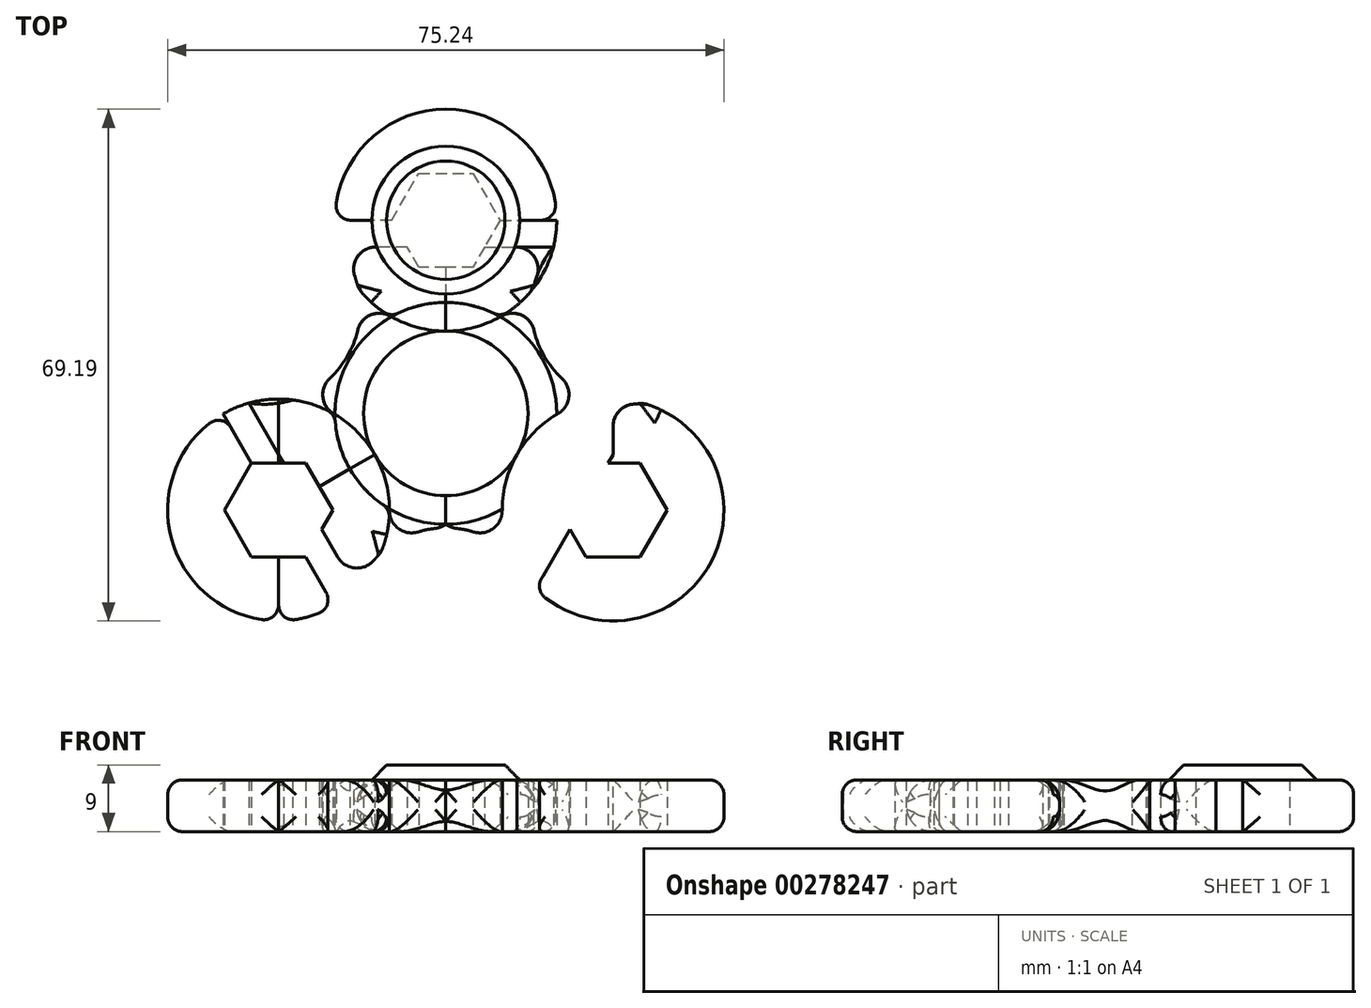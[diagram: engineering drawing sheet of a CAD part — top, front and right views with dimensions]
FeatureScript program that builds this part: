
annotation { "Feature Type Name" : "Feature", "Feature Type Description" : "" }
export const myFeature = defineFeature(function(context is Context, id is Id, definition is map)
    precondition{}
    {
        {
            var Q0;
            Q0=qCreatedBy(makeId("Top.planeOp"),FACE);
            var sketch = newSketch(context, id + "F0", { "sketchPlane" : qUnion([Q0])});
            skCircle(sketch, "E0", {"center": v(0, 26.12) * mm, "radius": 15 * mm});
            skLineSegment(sketch, "E1", {"start": v(0, 26.12) * mm, "end": v(0, -26.13) * mm});
            skLineSegment(sketch, "E2", {"start": v(0, 11.12) * mm, "end": v(0, 0) * mm});
            skCircle(sketch, "E3", {"center": v(0, 0) * mm, "radius": 15 * mm});
            skCircle(sketch, "E4", {"center": v(0, 0) * mm, "radius": 11.12 * mm});
            skCircle(sketch, "E5.1.1", {"center": v(-22.62, -13.06) * mm, "radius": 15 * mm});
            skCircle(sketch, "E5.2.1", {"center": v(22.62, -13.06) * mm, "radius": 15 * mm});
            skLineSegment(sketch, "E6", {"start": v(-22.62, -13.06) * mm, "end": v(-22.62, 15.78) * mm});
            skLineSegment(sketch, "E7", {"start": v(0, 26.12) * mm, "end": v(-15, 26.12) * mm});
            skLineSegment(sketch, "E8", {"start": v(-15, 26.12) * mm, "end": v(0, 26.12) * mm});
            skLineSegment(sketch, "E9", {"start": v(0, 26.12) * mm, "end": v(15, 26.12) * mm});
            skLineSegment(sketch, "E10", {"start": v(-22.62, -13.06) * mm, "end": v(-22.62, -28.06) * mm});
            skLineSegment(sketch, "E11", {"start": v(22.62, -13.06) * mm, "end": v(22.62, -28.06) * mm});
            skLineSegment(sketch, "E12", {"start": v(22.62, -28.06) * mm, "end": v(22.62, -13.06) * mm});
            skLineSegment(sketch, "E13", {"start": v(22.62, 1.94) * mm, "end": v(22.62, -13.06) * mm});
            skLineSegment(sketch, "E14", {"start": v(-22.62, -13.06) * mm, "end": v(-9.63, -5.56) * mm});
            skLineSegment(sketch, "E15", {"start": v(22.62, -13.06) * mm, "end": v(9.63, -5.56) * mm});
            skLineSegment(sketch, "E16", {"start": v(9.63, -5.56) * mm, "end": v(22.62, -13.06) * mm});
            skLineSegment(sketch, "E17", {"start": v(22.62, -13.06) * mm, "end": v(15.12, -26.05) * mm});
            skLineSegment(sketch, "E18", {"start": v(-22.62, -13.06) * mm, "end": v(-15.12, -26.05) * mm});
            skLineSegment(sketch, "E19", {"start": v(-15.12, -26.05) * mm, "end": v(-22.62, -13.06) * mm});
            skLineSegment(sketch, "E20", {"start": v(-22.62, -13.06) * mm, "end": v(-30.12, -0.07) * mm});
            skLineSegment(sketch, "E21", {"start": v(22.62, -13.06) * mm, "end": v(30.12, -0.07) * mm});
            skLineSegment(sketch, "E22", {"start": v(0, 26.12) * mm, "end": v(-11.55, 16.56) * mm, "construction": true});
            skLineSegment(sketch, "E23", {"start": v(-11.55, 16.56) * mm, "end": v(-5.78, 21.34) * mm, "construction": true});
            skLineSegment(sketch, "E24", {"start": v(22.62, -28.06) * mm, "end": v(15.12, -26.05) * mm});
            skLineSegment(sketch, "E25", {"start": v(22.62, -13.06) * mm, "end": v(16.13, -9.31) * mm});
            skLineSegment(sketch, "E26", {"start": v(13, -7.5) * mm, "end": v(19.38, -11.19) * mm});
            skLineSegment(sketch, "E27", {"start": v(19.38, -11.19) * mm, "end": v(12.12, -23.77) * mm});
            skLineSegment(sketch, "E28", {"start": v(-13, -7.5) * mm, "end": v(-19.38, -11.19) * mm});
            skLineSegment(sketch, "E29", {"start": v(-19.38, -11.19) * mm, "end": v(-12.12, -23.77) * mm});
            skLineSegment(sketch, "E30", {"start": v(-19.38, -11.19) * mm, "end": v(-26.64, 1.4) * mm});
            skLineSegment(sketch, "E31", {"start": v(19.38, -11.19) * mm, "end": v(26.64, 1.4) * mm});
            skLineSegment(sketch, "E32", {"start": v(0, 15) * mm, "end": v(0, 22.5) * mm});
            skLineSegment(sketch, "E33", {"start": v(0, 22.5) * mm, "end": v(-14.56, 22.5) * mm});
            skLineSegment(sketch, "E34", {"start": v(0, 22.5) * mm, "end": v(14.56, 22.5) * mm});
            skArc(sketch, "E35", {"start": v(12.12, -23.77) * mm, "mid": v(0, -15.48) * mm, "end": v(-12.12, -23.77) * mm});
            skArc(sketch, "E36", {"start": v(-26.64, 1.4) * mm, "mid": v(-13.3, 7.77) * mm, "end": v(-14.56, 22.5) * mm});
            skArc(sketch, "E37", {"start": v(14.56, 22.5) * mm, "mid": v(13.3, 7.77) * mm, "end": v(26.64, 1.4) * mm});
            skCircle(sketch, "E38.cCircle", {"center": v(-22.62, -13.06) * mm, "radius": 6.35 * mm, "construction": true});
            skLineSegment(sketch, "E38.0", {"start": v(-18.96, -6.71) * mm, "end": v(-15.3, -13.06) * mm});
            skLineSegment(sketch, "E38.1", {"start": v(-15.3, -13.06) * mm, "end": v(-18.96, -19.41) * mm});
            skLineSegment(sketch, "E38.2", {"start": v(-18.96, -19.41) * mm, "end": v(-26.3, -19.41) * mm});
            skLineSegment(sketch, "E38.3", {"start": v(-26.3, -19.41) * mm, "end": v(-29.96, -13.06) * mm});
            skLineSegment(sketch, "E38.4", {"start": v(-29.96, -13.06) * mm, "end": v(-26.3, -6.71) * mm});
            skLineSegment(sketch, "E38.5", {"start": v(-26.3, -6.71) * mm, "end": v(-18.96, -6.71) * mm});
            skPoint(sketch, "E38.0.midPoint", {"position": v(-17.13, -9.89) * mm});
            skCircle(sketch, "E39.cCircle", {"center": v(22.62, -13.06) * mm, "radius": 6.35 * mm, "construction": true});
            skLineSegment(sketch, "E39.0", {"start": v(15.3, -13.06) * mm, "end": v(18.96, -6.71) * mm});
            skLineSegment(sketch, "E39.1", {"start": v(18.96, -6.71) * mm, "end": v(26.3, -6.71) * mm});
            skLineSegment(sketch, "E39.2", {"start": v(26.3, -6.71) * mm, "end": v(29.96, -13.06) * mm});
            skLineSegment(sketch, "E39.3", {"start": v(29.96, -13.06) * mm, "end": v(26.3, -19.41) * mm});
            skLineSegment(sketch, "E39.4", {"start": v(26.3, -19.41) * mm, "end": v(18.96, -19.41) * mm});
            skLineSegment(sketch, "E39.5", {"start": v(18.96, -19.41) * mm, "end": v(15.3, -13.06) * mm});
            skPoint(sketch, "E39.0.midPoint", {"position": v(17.13, -9.89) * mm});
            skCircle(sketch, "E40.cCircle", {"center": v(0, 26.12) * mm, "radius": 6.35 * mm, "construction": true});
            skLineSegment(sketch, "E40.0", {"start": v(3.67, 19.77) * mm, "end": v(-3.67, 19.77) * mm});
            skLineSegment(sketch, "E40.1", {"start": v(-3.67, 19.77) * mm, "end": v(-7.33, 26.12) * mm});
            skLineSegment(sketch, "E40.2", {"start": v(-7.33, 26.12) * mm, "end": v(-3.67, 32.47) * mm});
            skLineSegment(sketch, "E40.3", {"start": v(-3.67, 32.48) * mm, "end": v(3.67, 32.48) * mm});
            skLineSegment(sketch, "E40.4", {"start": v(3.67, 32.47) * mm, "end": v(7.33, 26.12) * mm});
            skLineSegment(sketch, "E40.5", {"start": v(7.33, 26.12) * mm, "end": v(3.67, 19.77) * mm});
            skPoint(sketch, "E40.0.midPoint", {"position": v(0, 19.77) * mm});
            skSolve(sketch);
        }
        {
            var Q0;
            {var subQ0=sQuery(id+"F0.wireOp",EDGE,"E38.5");var subQ1=sQuery(id+"F0.wireOp",EDGE,"E6");var subQ2=makeQuery(id+"F0.imprint","INTERSECT",VERTEX,{"derivedFrom":[subQ1,subQ0]});Q0=makeQuery(id+"F0.imprint","IMPRINT",FACE,{"disambiguationData":[TD([[makeQuery(id+"F0.imprint","IMPRINT",EDGE,{"disambiguationData":[TD([[subQ2,-1.0]])],"derivedFrom":subQ1}),-1.0]])]});}
            var Q1;
            {var subQ0=sQuery(id+"F0.wireOp",EDGE,"E38.3");Q1=makeQuery(id+"F0.imprint","IMPRINT",FACE,{"disambiguationData":[TD([[makeQuery(id+"F0.imprint","IMPRINT",EDGE,{"derivedFrom":subQ0}),1.0]])]});}
            var Q2;
            {var subQ5=sQuery(id+"F0.wireOp",EDGE,"E36");var subQ6=sQuery(id+"F0.wireOp",EDGE,"E5.1.1");var subQ7=makeQuery(id+"F0.imprint","INTERSECT",VERTEX,{"derivedFrom":[subQ6,subQ5]});Q2=makeQuery(id+"F0.imprint","IMPRINT",FACE,{"disambiguationData":[TD([[makeQuery(id+"F0.imprint","IMPRINT",EDGE,{"disambiguationData":[TD([[subQ7,1.0]])],"derivedFrom":subQ6}),1.0]])]});}
            var Q3;
            {var subQ5=sQuery(id+"F0.wireOp",EDGE,"E5.1.1");var subQ7=sQuery(id+"F0.wireOp",EDGE,"E35");var subQ12=makeQuery(id+"F0.imprint","INTERSECT",VERTEX,{"derivedFrom":[subQ5,subQ7]});Q3=makeQuery(id+"F0.imprint","IMPRINT",FACE,{"disambiguationData":[TD([[makeQuery(id+"F0.imprint","IMPRINT",EDGE,{"disambiguationData":[TD([[subQ12,-1.0]])],"derivedFrom":subQ5}),1.0]])]});}
            var Q4;
            {var subQ1=sQuery(id+"F0.wireOp",EDGE,"E3");var subQ3=sQuery(id+"F0.wireOp",EDGE,"E5.1.1");var subQ4=makeQuery(id+"F0.imprint","INTERSECT",VERTEX,{"disambiguationData":[OD(1.0)],"derivedFrom":[subQ1,subQ3]});Q4=makeQuery(id+"F0.imprint","IMPRINT",FACE,{"disambiguationData":[TD([[makeQuery(id+"F0.imprint","IMPRINT",EDGE,{"disambiguationData":[TD([[subQ4,1.0]])],"derivedFrom":subQ1}),1.0]])]});}
            var Q5;
            {var subQ1=sQuery(id+"F0.wireOp",EDGE,"E3");var subQ3=sQuery(id+"F0.wireOp",EDGE,"E5.1.1");var subQ4=makeQuery(id+"F0.imprint","INTERSECT",VERTEX,{"disambiguationData":[OD(0.0)],"derivedFrom":[subQ1,subQ3]});Q5=makeQuery(id+"F0.imprint","IMPRINT",FACE,{"disambiguationData":[TD([[makeQuery(id+"F0.imprint","IMPRINT",EDGE,{"disambiguationData":[TD([[subQ4,-1.0]])],"derivedFrom":subQ1}),1.0]])]});}
            var Q6;
            {var subQ1=sQuery(id+"F0.wireOp",EDGE,"E0");var subQ3=sQuery(id+"F0.wireOp",EDGE,"E3");var subQ4=makeQuery(id+"F0.imprint","INTERSECT",VERTEX,{"disambiguationData":[OD(0.0)],"derivedFrom":[subQ1,subQ3]});Q6=makeQuery(id+"F0.imprint","IMPRINT",FACE,{"disambiguationData":[TD([[makeQuery(id+"F0.imprint","IMPRINT",EDGE,{"disambiguationData":[TD([[subQ4,-1.0]])],"derivedFrom":subQ3}),1.0]])]});}
            var Q7;
            {var subQ0=sQuery(id+"F0.wireOp",EDGE,"E36");var subQ1=sQuery(id+"F0.wireOp",EDGE,"E0");var subQ2=makeQuery(id+"F0.imprint","INTERSECT",VERTEX,{"derivedFrom":[subQ1,subQ0]});Q7=makeQuery(id+"F0.imprint","IMPRINT",FACE,{"disambiguationData":[TD([[makeQuery(id+"F0.imprint","IMPRINT",EDGE,{"disambiguationData":[TD([[subQ2,-1.0]])],"derivedFrom":subQ1}),-1.0]])]});}
            var Q8;
            {var subQ5=sQuery(id+"F0.wireOp",EDGE,"E0");var subQ11=sQuery(id+"F0.wireOp",EDGE,"E36");var subQ13=makeQuery(id+"F0.imprint","INTERSECT",VERTEX,{"derivedFrom":[subQ5,subQ11]});Q8=makeQuery(id+"F0.imprint","IMPRINT",FACE,{"disambiguationData":[TD([[makeQuery(id+"F0.imprint","IMPRINT",EDGE,{"disambiguationData":[TD([[subQ13,-1.0]])],"derivedFrom":subQ5}),1.0]])]});}
            var Q9;
            {var subQ0=sQuery(id+"F0.wireOp",EDGE,"E40.2");Q9=makeQuery(id+"F0.imprint","IMPRINT",FACE,{"disambiguationData":[TD([[makeQuery(id+"F0.imprint","IMPRINT",EDGE,{"derivedFrom":subQ0}),1.0]])]});}
            var Q10;
            {var subQ1=sQuery(id+"F0.wireOp",EDGE,"E0");var subQ3=sQuery(id+"F0.wireOp",EDGE,"E3");var subQ4=makeQuery(id+"F0.imprint","INTERSECT",VERTEX,{"disambiguationData":[OD(1.0)],"derivedFrom":[subQ1,subQ3]});Q10=makeQuery(id+"F0.imprint","IMPRINT",FACE,{"disambiguationData":[TD([[makeQuery(id+"F0.imprint","IMPRINT",EDGE,{"disambiguationData":[TD([[subQ4,-1.0]])],"derivedFrom":subQ3}),1.0]])]});}
            var Q11;
            {var subQ0=sQuery(id+"F0.wireOp",EDGE,"E37");var subQ2=sQuery(id+"F0.wireOp",EDGE,"E0");var subQ12=makeQuery(id+"F0.imprint","INTERSECT",VERTEX,{"derivedFrom":[subQ2,subQ0]});Q11=makeQuery(id+"F0.imprint","IMPRINT",FACE,{"disambiguationData":[TD([[makeQuery(id+"F0.imprint","IMPRINT",EDGE,{"disambiguationData":[TD([[subQ12,1.0]])],"derivedFrom":subQ2}),1.0]])]});}
            var Q12;
            {var subQ0=sQuery(id+"F0.wireOp",EDGE,"E37");var subQ1=sQuery(id+"F0.wireOp",EDGE,"E0");var subQ2=makeQuery(id+"F0.imprint","INTERSECT",VERTEX,{"derivedFrom":[subQ1,subQ0]});Q12=makeQuery(id+"F0.imprint","IMPRINT",FACE,{"disambiguationData":[TD([[makeQuery(id+"F0.imprint","IMPRINT",EDGE,{"disambiguationData":[TD([[subQ2,1.0]])],"derivedFrom":subQ1}),-1.0]])]});}
            var Q13;
            {var subQ1=sQuery(id+"F0.wireOp",EDGE,"E0");var subQ3=sQuery(id+"F0.wireOp",EDGE,"E3");var subQ4=makeQuery(id+"F0.imprint","INTERSECT",VERTEX,{"disambiguationData":[OD(1.0)],"derivedFrom":[subQ1,subQ3]});Q13=makeQuery(id+"F0.imprint","IMPRINT",FACE,{"disambiguationData":[TD([[makeQuery(id+"F0.imprint","IMPRINT",EDGE,{"disambiguationData":[TD([[subQ4,1.0]])],"derivedFrom":subQ3}),1.0]])]});}
            var Q14;
            {var subQ0=sQuery(id+"F0.wireOp",EDGE,"E4");var subQ1=sQuery(id+"F0.wireOp",EDGE,"E1");var subQ2=makeQuery(id+"F0.imprint","INTERSECT",VERTEX,{"derivedFrom":[subQ1,subQ0]});Q14=makeQuery(id+"F0.imprint","IMPRINT",FACE,{"disambiguationData":[TD([[makeQuery(id+"F0.imprint","IMPRINT",EDGE,{"disambiguationData":[TD([[subQ2,-1.0]])],"derivedFrom":subQ1}),1.0]])]});}
            var Q15;
            {var subQ0=sQuery(id+"F0.wireOp",EDGE,"E35");var subQ1=sQuery(id+"F0.wireOp",EDGE,"E1");var subQ2=makeQuery(id+"F0.imprint","INTERSECT",VERTEX,{"derivedFrom":[subQ1,subQ0]});Q15=makeQuery(id+"F0.imprint","IMPRINT",FACE,{"disambiguationData":[TD([[makeQuery(id+"F0.imprint","IMPRINT",EDGE,{"disambiguationData":[TD([[subQ2,1.0]])],"derivedFrom":subQ1}),1.0]])]});}
            var Q16;
            {var subQ0=sQuery(id+"F0.wireOp",EDGE,"E4");var subQ1=sQuery(id+"F0.wireOp",EDGE,"E1");var subQ2=makeQuery(id+"F0.imprint","INTERSECT",VERTEX,{"derivedFrom":[subQ1,subQ0]});Q16=makeQuery(id+"F0.imprint","IMPRINT",FACE,{"disambiguationData":[TD([[makeQuery(id+"F0.imprint","IMPRINT",EDGE,{"disambiguationData":[TD([[subQ2,-1.0]])],"derivedFrom":subQ1}),-1.0]])]});}
            var Q17;
            {var subQ0=sQuery(id+"F0.wireOp",EDGE,"E35");var subQ1=sQuery(id+"F0.wireOp",EDGE,"E1");var subQ2=makeQuery(id+"F0.imprint","INTERSECT",VERTEX,{"derivedFrom":[subQ1,subQ0]});Q17=makeQuery(id+"F0.imprint","IMPRINT",FACE,{"disambiguationData":[TD([[makeQuery(id+"F0.imprint","IMPRINT",EDGE,{"disambiguationData":[TD([[subQ2,1.0]])],"derivedFrom":subQ1}),-1.0]])]});}
            var Q18;
            {var subQ0=sQuery(id+"F0.wireOp",EDGE,"E24");Q18=makeQuery(id+"F0.imprint","IMPRINT",FACE,{"disambiguationData":[TD([[makeQuery(id+"F0.imprint","IMPRINT",EDGE,{"derivedFrom":subQ0}),-1.0]])]});}
            var Q19;
            {var subQ0=sQuery(id+"F0.wireOp",EDGE,"E24");Q19=makeQuery(id+"F0.imprint","IMPRINT",FACE,{"disambiguationData":[TD([[makeQuery(id+"F0.imprint","IMPRINT",EDGE,{"derivedFrom":subQ0}),1.0]])]});}
            var Q20;
            {var subQ0=sQuery(id+"F0.wireOp",EDGE,"E16");Q20=makeQuery(id+"F0.imprint","IMPRINT",FACE,{"disambiguationData":[TD([[makeQuery(id+"F0.imprint","IMPRINT",EDGE,{"derivedFrom":subQ0}),1.0]])]});}
            var Q21;
            {var subQ0=sQuery(id+"F0.wireOp",EDGE,"E39.2");Q21=makeQuery(id+"F0.imprint","IMPRINT",FACE,{"disambiguationData":[TD([[makeQuery(id+"F0.imprint","IMPRINT",EDGE,{"derivedFrom":subQ0}),1.0]])]});}
            var Q22;
            {var subQ0=sQuery(id+"F0.wireOp",EDGE,"E26");var subQ1=makeQuery(id+"F0.imprint","IMPRINT",VERTEX,{"derivedFrom":subQ0});Q22=makeQuery(id+"F0.imprint","IMPRINT",FACE,{"disambiguationData":[TD([[makeQuery(id+"F0.imprint","IMPRINT",EDGE,{"disambiguationData":[TD([[subQ1,-1.0]])],"derivedFrom":subQ0}),-1.0]])]});}
            var Q23;
            {var subQ5=sQuery(id+"F0.wireOp",EDGE,"E26");var subQ8=makeQuery(id+"F0.imprint","IMPRINT",VERTEX,{"derivedFrom":subQ5});Q23=makeQuery(id+"F0.imprint","IMPRINT",FACE,{"disambiguationData":[TD([[makeQuery(id+"F0.imprint","IMPRINT",EDGE,{"disambiguationData":[TD([[subQ8,-1.0]])],"derivedFrom":subQ5}),1.0]])]});}
            var Q24;
            {var subQ0=sQuery(id+"F0.wireOp",EDGE,"E16");Q24=makeQuery(id+"F0.imprint","IMPRINT",FACE,{"disambiguationData":[TD([[makeQuery(id+"F0.imprint","IMPRINT",EDGE,{"derivedFrom":subQ0}),-1.0]])]});}
            var Q25;
            {var subQ0=sQuery(id+"F0.wireOp",EDGE,"E31");var subQ1=sQuery(id+"F0.wireOp",EDGE,"E13");var subQ2=makeQuery(id+"F0.imprint","INTERSECT",VERTEX,{"derivedFrom":[subQ1,subQ0]});Q25=makeQuery(id+"F0.imprint","IMPRINT",FACE,{"disambiguationData":[TD([[makeQuery(id+"F0.imprint","IMPRINT",EDGE,{"disambiguationData":[TD([[subQ2,-1.0]])],"derivedFrom":subQ1}),-1.0]])]});}
            var Q26;
            {var subQ1=sQuery(id+"F0.wireOp",EDGE,"E0");var subQ3=sQuery(id+"F0.wireOp",EDGE,"E3");var subQ4=makeQuery(id+"F0.imprint","INTERSECT",VERTEX,{"disambiguationData":[OD(0.0)],"derivedFrom":[subQ1,subQ3]});Q26=makeQuery(id+"F0.imprint","IMPRINT",FACE,{"disambiguationData":[TD([[makeQuery(id+"F0.imprint","IMPRINT",EDGE,{"disambiguationData":[TD([[subQ4,1.0]])],"derivedFrom":subQ3}),1.0]])]});}
            var Q27;
            {var subQ0=sQuery(id+"F0.wireOp",EDGE,"E19");var subQ1=sQuery(id+"F0.wireOp",EDGE,"E5.1.1");var subQ2=makeQuery(id+"F0.imprint","INTERSECT",VERTEX,{"derivedFrom":[subQ1,subQ0]});Q27=makeQuery(id+"F0.imprint","IMPRINT",FACE,{"disambiguationData":[TD([[makeQuery(id+"F0.imprint","IMPRINT",EDGE,{"disambiguationData":[TD([[subQ2,-1.0]])],"derivedFrom":subQ1}),1.0]])]});}
            var Q28;
            {var subQ0=sQuery(id+"F0.wireOp",EDGE,"E10");var subQ1=sQuery(id+"F0.wireOp",EDGE,"E5.1.1");var subQ2=makeQuery(id+"F0.imprint","INTERSECT",VERTEX,{"derivedFrom":[subQ1,subQ0]});Q28=makeQuery(id+"F0.imprint","IMPRINT",FACE,{"disambiguationData":[TD([[makeQuery(id+"F0.imprint","IMPRINT",EDGE,{"disambiguationData":[TD([[subQ2,-1.0]])],"derivedFrom":subQ1}),1.0]])]});}
            var Q29;
            {var subQ3=sQuery(id+"F0.wireOp",EDGE,"E27");var subQ5=sQuery(id+"F0.wireOp",EDGE,"E39.5");var subQ7=makeQuery(id+"F0.imprint","INTERSECT",VERTEX,{"derivedFrom":[subQ3,subQ5]});Q29=makeQuery(id+"F0.imprint","IMPRINT",FACE,{"disambiguationData":[TD([[makeQuery(id+"F0.imprint","IMPRINT",EDGE,{"disambiguationData":[TD([[subQ7,-1.0]])],"derivedFrom":subQ3}),1.0]])]});}
            var Q30;
            {var subQ0=sQuery(id+"F0.wireOp",EDGE,"E9");var subQ1=sQuery(id+"F0.wireOp",EDGE,"E0");var subQ2=makeQuery(id+"F0.imprint","INTERSECT",VERTEX,{"derivedFrom":[subQ1,subQ0]});Q30=makeQuery(id+"F0.imprint","IMPRINT",FACE,{"disambiguationData":[TD([[makeQuery(id+"F0.imprint","IMPRINT",EDGE,{"disambiguationData":[TD([[subQ2,1.0]])],"derivedFrom":subQ1}),1.0]])]});}
            var Q31;
            {var subQ0=sQuery(id+"F0.wireOp",EDGE,"E31");var subQ3=sQuery(id+"F0.wireOp",EDGE,"E13");var subQ4=makeQuery(id+"F0.imprint","INTERSECT",VERTEX,{"derivedFrom":[subQ3,subQ0]});Q31=makeQuery(id+"F0.imprint","IMPRINT",FACE,{"disambiguationData":[TD([[makeQuery(id+"F0.imprint","IMPRINT",EDGE,{"disambiguationData":[TD([[subQ4,-1.0]])],"derivedFrom":subQ3}),1.0]])]});}
            var Q32;
            {var subQ0=sQuery(id+"F0.wireOp",EDGE,"E37");var subQ1=sQuery(id+"F0.wireOp",EDGE,"E13");var subQ2=makeQuery(id+"F0.imprint","INTERSECT",VERTEX,{"derivedFrom":[subQ1,subQ0]});Q32=makeQuery(id+"F0.imprint","IMPRINT",FACE,{"disambiguationData":[TD([[makeQuery(id+"F0.imprint","IMPRINT",EDGE,{"disambiguationData":[TD([[subQ2,-1.0]])],"derivedFrom":subQ1}),1.0]])]});}
            var Q33;
            {var subQ3=sQuery(id+"F0.wireOp",EDGE,"E6");var subQ7=sQuery(id+"F0.wireOp",EDGE,"E38.5");var subQ9=makeQuery(id+"F0.imprint","INTERSECT",VERTEX,{"derivedFrom":[subQ3,subQ7]});Q33=makeQuery(id+"F0.imprint","IMPRINT",FACE,{"disambiguationData":[TD([[makeQuery(id+"F0.imprint","IMPRINT",EDGE,{"disambiguationData":[TD([[subQ9,-1.0]])],"derivedFrom":subQ3}),1.0]])]});}
            var Q34;
            {var subQ0=sQuery(id+"F0.wireOp",EDGE,"E30");var subQ1=sQuery(id+"F0.wireOp",EDGE,"E6");var subQ2=makeQuery(id+"F0.imprint","INTERSECT",VERTEX,{"derivedFrom":[subQ1,subQ0]});Q34=makeQuery(id+"F0.imprint","IMPRINT",FACE,{"disambiguationData":[TD([[makeQuery(id+"F0.imprint","IMPRINT",EDGE,{"disambiguationData":[TD([[subQ2,-1.0]])],"derivedFrom":subQ1}),1.0]])]});}
            var Q35;
            {var subQ0=sQuery(id+"F0.wireOp",EDGE,"E8");var subQ1=sQuery(id+"F0.wireOp",EDGE,"E0");var subQ2=makeQuery(id+"F0.imprint","INTERSECT",VERTEX,{"derivedFrom":[subQ1,subQ0]});Q35=makeQuery(id+"F0.imprint","IMPRINT",FACE,{"disambiguationData":[TD([[makeQuery(id+"F0.imprint","IMPRINT",EDGE,{"disambiguationData":[TD([[subQ2,-1.0]])],"derivedFrom":subQ1}),1.0]])]});}
            extrude(context, id + "F1", {"entities" : qUnion([Q0, Q1, Q2, Q3, Q4, Q5, Q6, Q7, Q8, Q9, Q10, Q11, Q12, Q13, Q14, Q15, Q16, Q17, Q18, Q19, Q20, Q21, Q22, Q23, Q24, Q25, Q26, Q27, Q28, Q29, Q30, Q31, Q32, Q33, Q34, Q35]), "depth" : 7 * mm, "offsetDistance" : 25 * mm});
        }
        {
            var Q0;
            Q0=makeQuery(id+"F1.opExtrude","SWEPT_FACE",FACE,{"disambiguationData":[OSD([sQuery(id+"F0.wireOp",EDGE,"E35")])]});
            var Q1;
            Q1=makeQuery(id+"F1.opExtrude","SWEPT_FACE",FACE,{"disambiguationData":[OSD([sQuery(id+"F0.wireOp",EDGE,"E37")])]});
            var Q2;
            Q2=makeQuery(id+"F1.opExtrude","SWEPT_FACE",FACE,{"disambiguationData":[OSD([sQuery(id+"F0.wireOp",EDGE,"E36")])]});
            fillet(context, id + "F2", {"entities" : qUnion([Q0, Q1, Q2]), "radius" : 3 * mm, "tangentPropagation" : true, "allowEdgeOverflow" : false});
        }
        {
            var Q0;
            Q0=makeQuery(id+"F1.opExtrude","SWEPT_FACE",FACE,{"disambiguationData":[OSD([sQuery(id+"F0.wireOp",EDGE,"E5.1.1")])]});
            var Q1;
            Q1=makeQuery(id+"F1.opExtrude","SWEPT_FACE",FACE,{"disambiguationData":[OSD([sQuery(id+"F0.wireOp",EDGE,"E0")])]});
            var Q2;
            Q2=makeQuery(id+"F1.opExtrude","SWEPT_FACE",FACE,{"disambiguationData":[OSD([sQuery(id+"F0.wireOp",EDGE,"E5.2.1")])]});
            fillet(context, id + "F3", {"entities" : qUnion([Q0, Q1, Q2]), "radius" : 2 * mm, "tangentPropagation" : true, "allowEdgeOverflow" : false});
        }
        {
            var Q0;
            Q0=makeQuery(id+"F1.opExtrude","CAP_FACE",FACE,{"disambiguationData":[OSD([sQuery(id+"F0.wireOp",EDGE,"E0"),sQuery(id+"F0.wireOp",EDGE,"E4"),sQuery(id+"F0.wireOp",EDGE,"E5.1.1"),sQuery(id+"F0.wireOp",EDGE,"E5.2.1"),sQuery(id+"F0.wireOp",EDGE,"E35"),sQuery(id+"F0.wireOp",EDGE,"E36"),sQuery(id+"F0.wireOp",EDGE,"E37"),sQuery(id+"F0.wireOp",EDGE,"E38.0"),sQuery(id+"F0.wireOp",EDGE,"E38.1"),sQuery(id+"F0.wireOp",EDGE,"E38.2"),sQuery(id+"F0.wireOp",EDGE,"E38.3"),sQuery(id+"F0.wireOp",EDGE,"E38.4"),sQuery(id+"F0.wireOp",EDGE,"E38.5"),sQuery(id+"F0.wireOp",EDGE,"E39.0"),sQuery(id+"F0.wireOp",EDGE,"E39.1"),sQuery(id+"F0.wireOp",EDGE,"E39.2"),sQuery(id+"F0.wireOp",EDGE,"E39.3"),sQuery(id+"F0.wireOp",EDGE,"E39.4"),sQuery(id+"F0.wireOp",EDGE,"E39.5"),sQuery(id+"F0.wireOp",EDGE,"E40.0"),sQuery(id+"F0.wireOp",EDGE,"E40.1"),sQuery(id+"F0.wireOp",EDGE,"E40.2"),sQuery(id+"F0.wireOp",EDGE,"E40.3"),sQuery(id+"F0.wireOp",EDGE,"E40.4"),sQuery(id+"F0.wireOp",EDGE,"E40.5")])],"isStart":false});
            var sketch = newSketch(context, id + "F4", { "sketchPlane" : qUnion([Q0])});
            skCircle(sketch, "E41", {"center": v(0, 26.12) * mm, "radius": 10 * mm});
            skSolve(sketch);
        }
        {
            var Q0;
            Q0=makeQuery(id+"F4.imprint","IMPRINT",FACE,{"disambiguationData":[TD([[makeQuery(id+"F4.imprint","IMPRINT",EDGE,{"derivedFrom":sQuery(id+"F4.wireOp",EDGE,"E41")}),1.0]])]});
            var Q1;
            Q1=makeQuery(id+"F4.imprint","IMPRINT",FACE,{"disambiguationData":[TD([[makeQuery(id+"F4.imprint","IMPRINT",EDGE,{"derivedFrom":makeQuery(id+"F1.opExtrude","CAP_EDGE",EDGE,{"disambiguationData":[OSD([sQuery(id+"F0.wireOp",EDGE,"E40.0")])],"isStart":false})}),-1.0]])]});
            extrude(context, id + "F5", {"entities" : qUnion([Q0, Q1]), "depth" : 2 * mm, "offsetDistance" : 25 * mm});
        }
        {
            var Q0;
            Q0=makeQuery(id+"F5.opExtrude","CAP_EDGE",EDGE,{"disambiguationData":[OSD([sQuery(id+"F4.wireOp",EDGE,"E41")])],"isStart":false});
            chamfer(context, id + "F6", {"entities" : qUnion([Q0]), "width" : 2 * mm, "tangentPropagation" : true});
        }
    });
